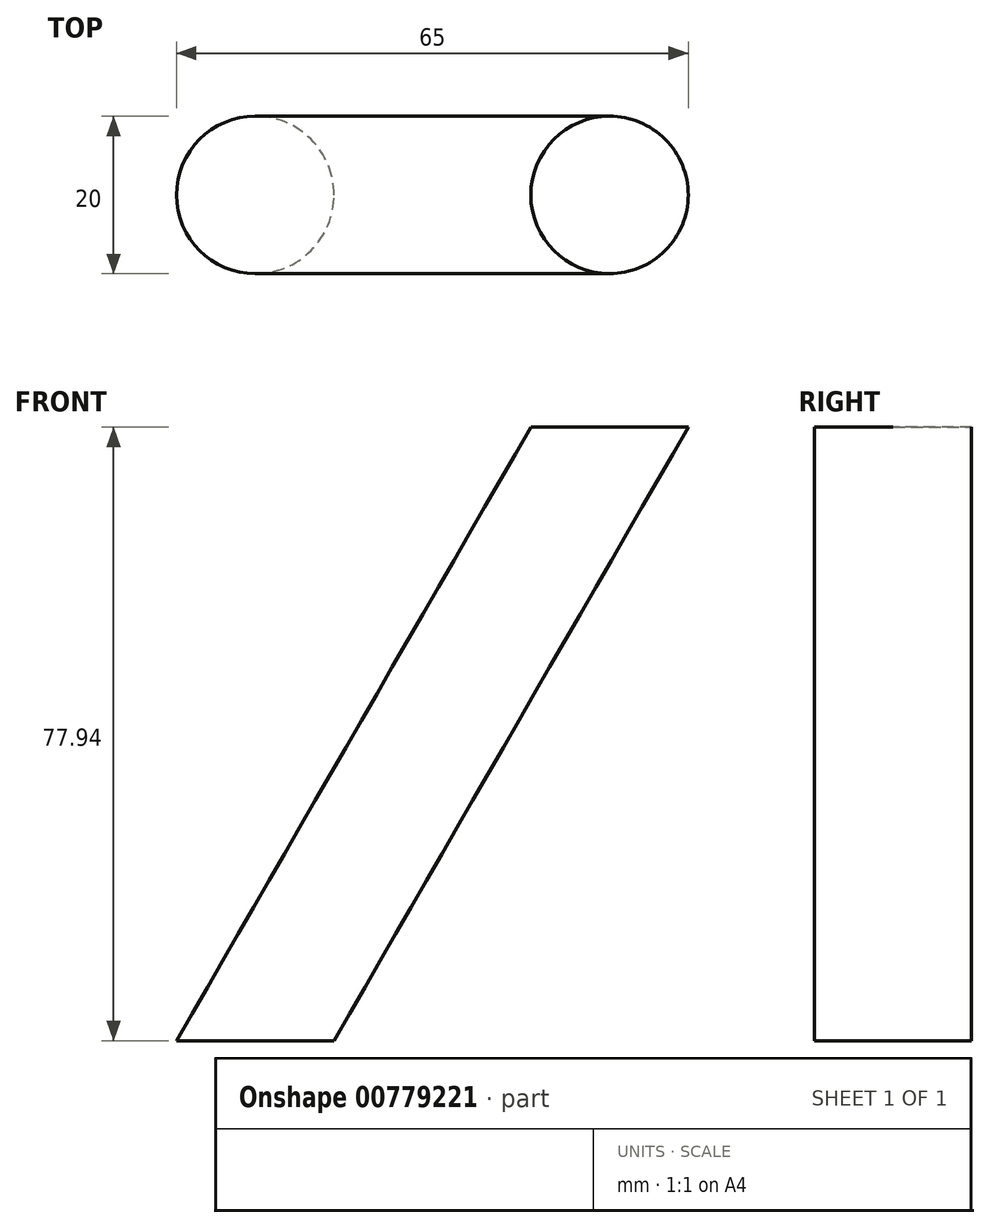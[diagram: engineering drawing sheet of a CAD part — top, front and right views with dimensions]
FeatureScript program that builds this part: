
annotation { "Feature Type Name" : "Feature", "Feature Type Description" : "" }
export const myFeature = defineFeature(function(context is Context, id is Id, definition is map)
    precondition{}
    {
        {
            var Q0;
            Q0=qCreatedBy(makeId("Top.planeOp"),FACE);
            var sketch = newSketch(context, id + "F0", { "sketchPlane" : qUnion([Q0])});
            skCircle(sketch, "E0", {"center": v(0, 0) * mm, "radius": 10 * mm});
            skSolve(sketch);
        }
        {
            var Q0;
            Q0=qCreatedBy(makeId("Front.planeOp"),FACE);
            var sketch = newSketch(context, id + "F1", { "sketchPlane" : qUnion([Q0])});
            skLineSegment(sketch, "E1", {"start": v(0, 0) * mm, "end": v(45, 77.94) * mm});
            skSolve(sketch);
        }
        {
            var Q0;
            Q0=makeQuery(id+"F0.imprint","IMPRINT",FACE,{"disambiguationData":[TD([[makeQuery(id+"F0.imprint","IMPRINT",EDGE,{"derivedFrom":sQuery(id+"F0.wireOp",EDGE,"E0")}),1.0]])]});
            var Q1;
            Q1=sQuery(id+"F1.wireOp",EDGE,"E1");
            sweep(context, id + "F2", {"profiles" : qUnion([Q0]), "path" : qUnion([Q1])});
        }
    });
